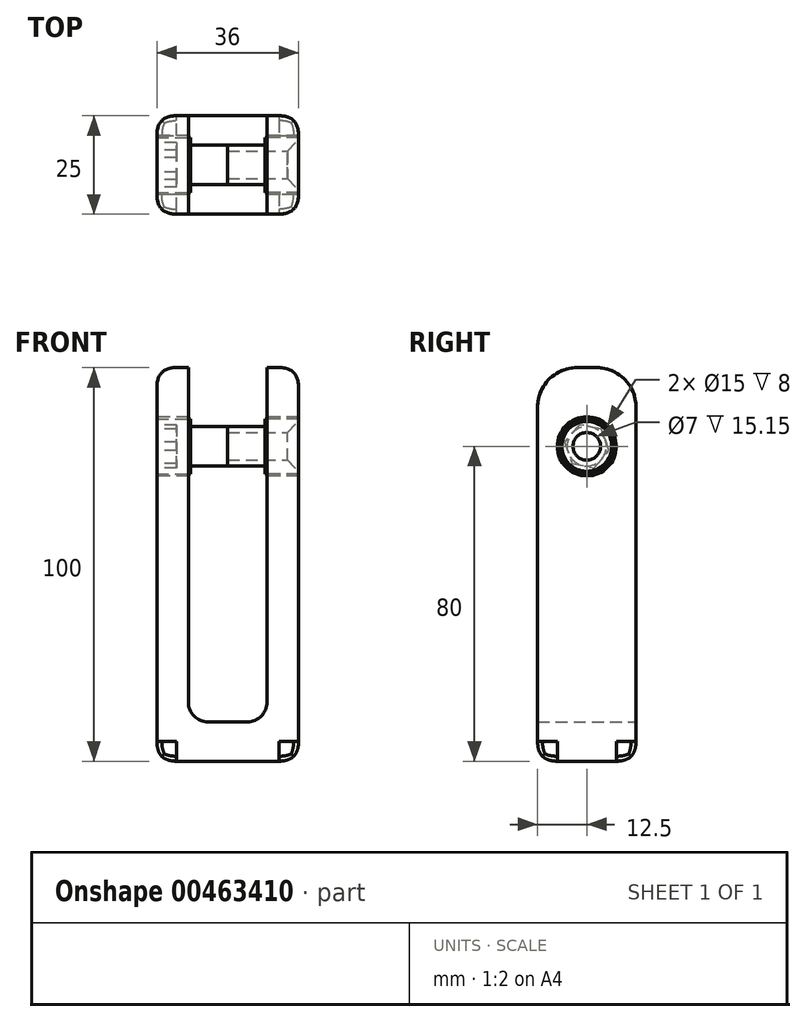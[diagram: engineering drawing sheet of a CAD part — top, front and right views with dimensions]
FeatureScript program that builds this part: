
annotation { "Feature Type Name" : "Feature", "Feature Type Description" : "" }
export const myFeature = defineFeature(function(context is Context, id is Id, definition is map)
    precondition{}
    {
        {
            var Q0;
            Q0=qCreatedBy(makeId("Front.planeOp"),FACE);
            var sketch = newSketch(context, id + "F0", { "sketchPlane" : qUnion([Q0])});
            skLineSegment(sketch, "E0", {"start": v(-18, 0) * mm, "end": v(-18, 100) * mm});
            skLineSegment(sketch, "E1", {"start": v(-18, 100) * mm, "end": v(-10, 100) * mm});
            skLineSegment(sketch, "E2", {"start": v(-10, 100) * mm, "end": v(-10, 10) * mm});
            skLineSegment(sketch, "E3", {"start": v(-10, 10) * mm, "end": v(0, 10) * mm});
            skLineSegment(sketch, "E4", {"start": v(0, 10) * mm, "end": v(0, 0) * mm});
            skLineSegment(sketch, "E5", {"start": v(-18, 0) * mm, "end": v(0, 0) * mm});
            skSolve(sketch);
        }
        {
            var Q0;
            Q0 = qSketchRegion(id + "F0", true);
            extrude(context, id + "F1", {"entities" : qUnion([Q0]), "depth" : 25 * mm});
        }
        {
            var Q0;
            Q0=makeQuery(id+"F1.opExtrude","SWEPT_BODY",BODY,{"disambiguationData":[OSD([sQuery(id+"F0.wireOp",EDGE,"E0"),sQuery(id+"F0.wireOp",EDGE,"E1"),sQuery(id+"F0.wireOp",EDGE,"E2"),sQuery(id+"F0.wireOp",EDGE,"E3"),sQuery(id+"F0.wireOp",EDGE,"E4"),sQuery(id+"F0.wireOp",EDGE,"E5")])]});
            var Q1;
            Q1=qCreatedBy(makeId("Right.planeOp"),FACE);
            mirror(context, id + "F2", {"operationType" : NewBodyOperationType.ADD, "entities" : qUnion([Q0]), "mirrorPlane" : qUnion([Q1])});
        }
        {
            var Q0;
            Q0=makeQuery(id+"F1.opExtrude","SWEPT_FACE",FACE,{"disambiguationData":[OSD([sQuery(id+"F0.wireOp",EDGE,"E0")])]});
            var sketch = newSketch(context, id + "F3", { "sketchPlane" : qUnion([Q0])});
            skPoint(sketch, "E6", {"position": v(12.5, 80) * mm});
            skSolve(sketch);
        }
        {
            var Q0;
            Q0=sQuery(id+"F3.wireOp",VERTEX,"E6");
            var Q1;
            Q1=makeQuery(id+"F1.opExtrude","SWEPT_BODY",BODY,{"disambiguationData":[OSD([sQuery(id+"F0.wireOp",EDGE,"E0"),sQuery(id+"F0.wireOp",EDGE,"E1"),sQuery(id+"F0.wireOp",EDGE,"E2"),sQuery(id+"F0.wireOp",EDGE,"E3"),sQuery(id+"F0.wireOp",EDGE,"E4"),sQuery(id+"F0.wireOp",EDGE,"E5")])]});
            hole(context, id + "F4", {"style" : HoleStyle.SIMPLE, "endStyle" : HoleEndStyle.THROUGH, "holeDiameter" : 15 * mm, "isTappedThrough" : true, "tappedDepth" : 12.7 * mm, "tapClearance" : 3, "locations" : qUnion([Q0]), "scope" : qUnion([Q1])});
        }
        {
            var Q0;
            Q0=makeQuery(id+"F2.opPattern","COPY",EDGE,{"derivedFrom":makeQuery(id+"F1.opExtrude","CAP_EDGE",EDGE,{"disambiguationData":[OSD([sQuery(id+"F0.wireOp",EDGE,"E1")])],"isStart":true}),"instanceName":"1"});
            var Q1;
            Q1=makeQuery(id+"F2.opPattern","COPY",EDGE,{"derivedFrom":makeQuery(id+"F1.opExtrude","CAP_EDGE",EDGE,{"disambiguationData":[OSD([sQuery(id+"F0.wireOp",EDGE,"E1")])],"isStart":false}),"instanceName":"1"});
            var Q2;
            Q2=makeQuery(id+"F1.opExtrude","CAP_EDGE",EDGE,{"disambiguationData":[OSD([sQuery(id+"F0.wireOp",EDGE,"E1")])],"isStart":true});
            var Q3;
            Q3=makeQuery(id+"F1.opExtrude","CAP_EDGE",EDGE,{"disambiguationData":[OSD([sQuery(id+"F0.wireOp",EDGE,"E1")])],"isStart":false});
            fillet(context, id + "F5", {"entities" : qUnion([Q0, Q1, Q2, Q3]), "radius" : 10 * mm, "tangentPropagation" : true, "allowEdgeOverflow" : false});
        }
        {
            var Q0;
            {var subQ0=makeQuery(id+"F1.opExtrude","CAP_EDGE",EDGE,{"disambiguationData":[OSD([sQuery(id+"F0.wireOp",EDGE,"E5")])],"isStart":true});Q0=makeQuery(id+"F2.boolean.opBoolean","MERGE",EDGE,{"derivedFrom":[subQ0,makeQuery(id+"F2.opPattern","COPY",EDGE,{"derivedFrom":subQ0,"instanceName":"1"})]});}
            var Q1;
            Q1=makeQuery(id+"F2.opPattern","COPY",EDGE,{"derivedFrom":makeQuery(id+"F1.opExtrude","CAP_EDGE",EDGE,{"disambiguationData":[OSD([sQuery(id+"F0.wireOp",EDGE,"E0")])],"isStart":true}),"instanceName":"1"});
            var Q2;
            Q2=makeQuery(id+"F5.opFillet","BLEND_EDGE",EDGE,{"blendedFrom":[makeQuery(id+"F2.opPattern","COPY",EDGE,{"derivedFrom":makeQuery(id+"F1.opExtrude","CAP_EDGE",EDGE,{"disambiguationData":[OSD([sQuery(id+"F0.wireOp",EDGE,"E1")])],"isStart":true}),"instanceName":"1"}),makeQuery(id+"F2.opPattern","COPY",FACE,{"derivedFrom":makeQuery(id+"F1.opExtrude","SWEPT_FACE",FACE,{"disambiguationData":[OSD([sQuery(id+"F0.wireOp",EDGE,"E0")])]}),"instanceName":"1"})],"blendedInto":[makeQuery(id+"F2.opPattern","COPY",FACE,{"derivedFrom":makeQuery(id+"F1.opExtrude","SWEPT_FACE",FACE,{"disambiguationData":[OSD([sQuery(id+"F0.wireOp",EDGE,"E0")])]}),"instanceName":"1"})]});
            var Q3;
            Q3=makeQuery(id+"F5.opFillet","BLEND_EDGE",EDGE,{"blendedFrom":[makeQuery(id+"F2.opPattern","COPY",EDGE,{"derivedFrom":makeQuery(id+"F1.opExtrude","CAP_EDGE",EDGE,{"disambiguationData":[OSD([sQuery(id+"F0.wireOp",EDGE,"E1")])],"isStart":false}),"instanceName":"1"}),makeQuery(id+"F2.opPattern","COPY",FACE,{"derivedFrom":makeQuery(id+"F1.opExtrude","SWEPT_FACE",FACE,{"disambiguationData":[OSD([sQuery(id+"F0.wireOp",EDGE,"E0")])]}),"instanceName":"1"})],"blendedInto":[makeQuery(id+"F2.opPattern","COPY",FACE,{"derivedFrom":makeQuery(id+"F1.opExtrude","SWEPT_FACE",FACE,{"disambiguationData":[OSD([sQuery(id+"F0.wireOp",EDGE,"E0")])]}),"instanceName":"1"})]});
            var Q4;
            Q4=makeQuery(id+"F2.opPattern","COPY",EDGE,{"derivedFrom":makeQuery(id+"F1.opExtrude","SWEPT_EDGE",EDGE,{"disambiguationData":[OSD([sQuery(id+"F0.wireOp",EDGE,"E0"),sQuery(id+"F0.wireOp",EDGE,"E1")])]}),"instanceName":"1"});
            var Q5;
            Q5=makeQuery(id+"F2.opPattern","COPY",EDGE,{"derivedFrom":makeQuery(id+"F1.opExtrude","CAP_EDGE",EDGE,{"disambiguationData":[OSD([sQuery(id+"F0.wireOp",EDGE,"E0")])],"isStart":false}),"instanceName":"1"});
            var Q6;
            Q6=makeQuery(id+"F2.opPattern","COPY",EDGE,{"derivedFrom":makeQuery(id+"F1.opExtrude","SWEPT_EDGE",EDGE,{"disambiguationData":[OSD([sQuery(id+"F0.wireOp",EDGE,"E0"),sQuery(id+"F0.wireOp",EDGE,"E5")])]}),"instanceName":"1"});
            var Q7;
            {var subQ0=makeQuery(id+"F1.opExtrude","CAP_EDGE",EDGE,{"disambiguationData":[OSD([sQuery(id+"F0.wireOp",EDGE,"E5")])],"isStart":false});Q7=makeQuery(id+"F2.boolean.opBoolean","MERGE",EDGE,{"derivedFrom":[subQ0,makeQuery(id+"F2.opPattern","COPY",EDGE,{"derivedFrom":subQ0,"instanceName":"1"})]});}
            var Q8;
            Q8=makeQuery(id+"F1.opExtrude","CAP_EDGE",EDGE,{"disambiguationData":[OSD([sQuery(id+"F0.wireOp",EDGE,"E0")])],"isStart":false});
            var Q9;
            Q9=makeQuery(id+"F5.opFillet","BLEND_EDGE",EDGE,{"blendedFrom":[makeQuery(id+"F1.opExtrude","CAP_EDGE",EDGE,{"disambiguationData":[OSD([sQuery(id+"F0.wireOp",EDGE,"E1")])],"isStart":true}),makeQuery(id+"F1.opExtrude","SWEPT_FACE",FACE,{"disambiguationData":[OSD([sQuery(id+"F0.wireOp",EDGE,"E0")])]})],"blendedInto":[makeQuery(id+"F1.opExtrude","SWEPT_FACE",FACE,{"disambiguationData":[OSD([sQuery(id+"F0.wireOp",EDGE,"E0")])]})]});
            var Q10;
            Q10=makeQuery(id+"F1.opExtrude","SWEPT_EDGE",EDGE,{"disambiguationData":[OSD([sQuery(id+"F0.wireOp",EDGE,"E0"),sQuery(id+"F0.wireOp",EDGE,"E1")])]});
            var Q11;
            Q11=makeQuery(id+"F5.opFillet","BLEND_EDGE",EDGE,{"blendedFrom":[makeQuery(id+"F1.opExtrude","CAP_EDGE",EDGE,{"disambiguationData":[OSD([sQuery(id+"F0.wireOp",EDGE,"E1")])],"isStart":false}),makeQuery(id+"F1.opExtrude","SWEPT_FACE",FACE,{"disambiguationData":[OSD([sQuery(id+"F0.wireOp",EDGE,"E0")])]})],"blendedInto":[makeQuery(id+"F1.opExtrude","SWEPT_FACE",FACE,{"disambiguationData":[OSD([sQuery(id+"F0.wireOp",EDGE,"E0")])]})]});
            var Q12;
            Q12=makeQuery(id+"F1.opExtrude","SWEPT_EDGE",EDGE,{"disambiguationData":[OSD([sQuery(id+"F0.wireOp",EDGE,"E0"),sQuery(id+"F0.wireOp",EDGE,"E5")])]});
            var Q13;
            Q13=makeQuery(id+"F1.opExtrude","CAP_EDGE",EDGE,{"disambiguationData":[OSD([sQuery(id+"F0.wireOp",EDGE,"E0")])],"isStart":true});
            fillet(context, id + "F6", {"entities" : qUnion([Q0, Q1, Q2, Q3, Q4, Q5, Q6, Q7, Q8, Q9, Q10, Q11, Q12, Q13]), "radius" : 5 * mm, "tangentPropagation" : true, "rho" : 0.5, "crossSection" : FilletCrossSection.CONIC, "allowEdgeOverflow" : false});
        }
        {
            var Q0;
            Q0=makeQuery(id+"F1.opExtrude","SWEPT_EDGE",EDGE,{"disambiguationData":[OSD([sQuery(id+"F0.wireOp",EDGE,"E2"),sQuery(id+"F0.wireOp",EDGE,"E3")])]});
            var Q1;
            Q1=makeQuery(id+"F2.opPattern","COPY",EDGE,{"derivedFrom":makeQuery(id+"F1.opExtrude","SWEPT_EDGE",EDGE,{"disambiguationData":[OSD([sQuery(id+"F0.wireOp",EDGE,"E2"),sQuery(id+"F0.wireOp",EDGE,"E3")])]}),"instanceName":"1"});
            fillet(context, id + "F7", {"entities" : qUnion([Q0, Q1]), "radius" : 5 * mm, "tangentPropagation" : true, "allowEdgeOverflow" : false});
        }
        {
            var Q0;
            Q0=qCreatedBy(makeId("Right.planeOp"),FACE);
            var sketch = newSketch(context, id + "F8", { "sketchPlane" : qUnion([Q0])});
            skCircle(sketch, "E7", {"center": v(-12.5, 80) * mm, "radius": 5 * mm});
            skSolve(sketch);
        }
        {
            var Q0;
            Q0=makeQuery(id+"F8.imprint","IMPRINT",FACE,{"disambiguationData":[TD([[makeQuery(id+"F8.imprint","IMPRINT",EDGE,{"derivedFrom":sQuery(id+"F8.wireOp",EDGE,"E7")}),1.0]])]});
            extrude(context, id + "F9", {"entities" : qUnion([Q0]), "depth" : 9.5 * mm});
        }
        {
            var Q0;
            Q0=makeQuery(id+"F9.opExtrude","CAP_FACE",FACE,{"disambiguationData":[OSD([sQuery(id+"F8.wireOp",EDGE,"E7")])],"isStart":false});
            var sketch = newSketch(context, id + "F10", { "sketchPlane" : qUnion([Q0])});
            skCircle(sketch, "E8", {"center": v(-12.5, 80) * mm, "radius": 7 * mm});
            skSolve(sketch);
        }
        {
            var Q0;
            Q0 = qSketchRegion(id + "F10", true);
            var Q1;
            Q1=makeQuery(id+"F6.opFillet","SPLIT",FACE,{"disambiguationData":[OD(1.0)],"derivedFrom":makeQuery(id+"F2.opPattern","COPY",FACE,{"derivedFrom":makeQuery(id+"F1.opExtrude","SWEPT_FACE",FACE,{"disambiguationData":[OSD([sQuery(id+"F0.wireOp",EDGE,"E0")])]}),"instanceName":"1"})});
            extrude(context, id + "F11", {"entities" : qUnion([Q0]), "operationType" : NewBodyOperationType.ADD, "endBound" : BoundingType.UP_TO_SURFACE, "endBoundEntityFace" : qUnion([Q1]), "depth" : 25.4 * mm});
        }
        {
            var Q0;
            Q0=makeQuery(id+"F9.opExtrude","SWEPT_BODY",BODY,{"disambiguationData":[OSD([sQuery(id+"F8.wireOp",EDGE,"E7")])]});
            var Q1;
            Q1=qCreatedBy(makeId("Right.planeOp"),FACE);
            mirror(context, id + "F12", {"operationType" : NewBodyOperationType.ADD, "entities" : qUnion([Q0]), "mirrorPlane" : qUnion([Q1])});
        }
        {
            var Q0;
            Q0=makeQuery(id+"F11.opExtrude","CAP_FACE",FACE,{"disambiguationData":[OSD([sQuery(id+"F10.wireOp",EDGE,"E8")])],"isStart":false});
            var sketch = newSketch(context, id + "F13", { "sketchPlane" : qUnion([Q0])});
            skPoint(sketch, "E9", {"position": v(-12.5, 80) * mm});
            skSolve(sketch);
        }
        {
            var Q0;
            Q0=sQuery(id+"F13.wireOp",VERTEX,"E9");
            var Q1;
            Q1=makeQuery(id+"F9.opExtrude","SWEPT_BODY",BODY,{"disambiguationData":[OSD([sQuery(id+"F8.wireOp",EDGE,"E7")])]});
            hole(context, id + "F14", {"style" : HoleStyle.C_SINK, "endStyle" : HoleEndStyle.THROUGH, "holeDiameter" : 7 * mm, "cSinkDiameter" : 12.7 * mm, "cSinkAngle" : 90 * degree, "isTappedThrough" : true, "tappedDepth" : 12.7 * mm, "tapClearance" : 3, "locations" : qUnion([Q0]), "scope" : qUnion([Q1])});
        }
        {
            var Q0;
            Q0=makeQuery(id+"F12.opPattern","COPY",FACE,{"derivedFrom":makeQuery(id+"F11.opExtrude","CAP_FACE",FACE,{"disambiguationData":[OSD([sQuery(id+"F10.wireOp",EDGE,"E8")])],"isStart":false}),"instanceName":"1"});
            var sketch = newSketch(context, id + "F15", { "sketchPlane" : qUnion([Q0])});
            skCircle(sketch, "E10.cCircle", {"center": v(12.5, 80) * mm, "radius": 5 * mm, "construction": true});
            skLineSegment(sketch, "E10.0", {"start": v(6.83, 78.9) * mm, "end": v(8.71, 84.36) * mm});
            skLineSegment(sketch, "E10.1", {"start": v(8.71, 84.36) * mm, "end": v(14.38, 85.46) * mm});
            skLineSegment(sketch, "E10.2", {"start": v(14.38, 85.46) * mm, "end": v(18.17, 81.1) * mm});
            skLineSegment(sketch, "E10.3", {"start": v(18.17, 81.1) * mm, "end": v(16.29, 75.64) * mm});
            skLineSegment(sketch, "E10.4", {"start": v(16.29, 75.64) * mm, "end": v(10.62, 74.54) * mm});
            skLineSegment(sketch, "E10.5", {"start": v(10.62, 74.54) * mm, "end": v(6.83, 78.9) * mm});
            skPoint(sketch, "E10.0.midPoint", {"position": v(7.77, 81.63) * mm});
            skSolve(sketch);
        }
        {
            var Q0;
            Q0=makeQuery(id+"F15.imprint","IMPRINT",FACE,{"disambiguationData":[TD([[makeQuery(id+"F15.imprint","IMPRINT",EDGE,{"derivedFrom":sQuery(id+"F15.wireOp",EDGE,"E10.0")}),-1.0]])]});
            extrude(context, id + "F16", {"entities" : qUnion([Q0]), "operationType" : NewBodyOperationType.REMOVE, "oppositeDirection" : true, "depth" : 5 * mm});
        }
    });
